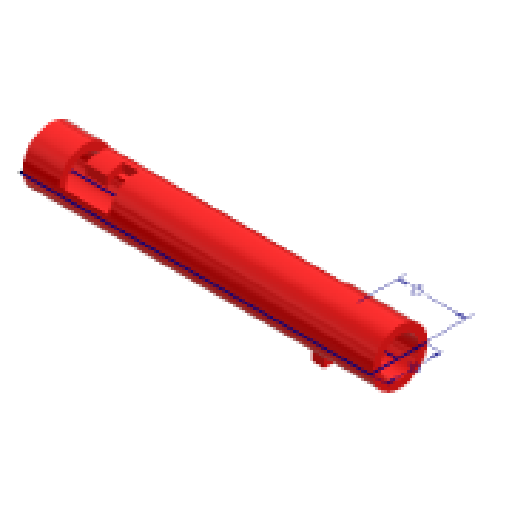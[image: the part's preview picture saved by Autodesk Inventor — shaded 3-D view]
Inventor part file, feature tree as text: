
AUTODESK INVENTOR PART (.ipt)
format: ipt  version: 2024 (Build 280153000, 153)  size: 166,400 bytes
history: native  units: mm
features: sketch x4, extrude x3, other x2, shell x1
ambient origin geometry x8: Origin, YZ Plane, XZ Plane, XY Plane, X Axis, Y Axis, Z Axis, Center Point
bodies: Solido1 (feature_tree)
feature tree (10):
  extrude  "Estrusione1"  Depth=20.0mm
  shell  "Svuotamento1"  Thickness=25.0mm
  sketch  "Schizzo1"
  other  "Piano di lavoro7"
  extrude  "Estrusione7"  Depth=11.0mm
  other  "Piano di lavoro8"
  extrude  "Estrusione8"  Depth=20.0mm
  sketch  "Schizzo2"
  sketch  "Schizzo13"
  sketch  "Schizzo14"
